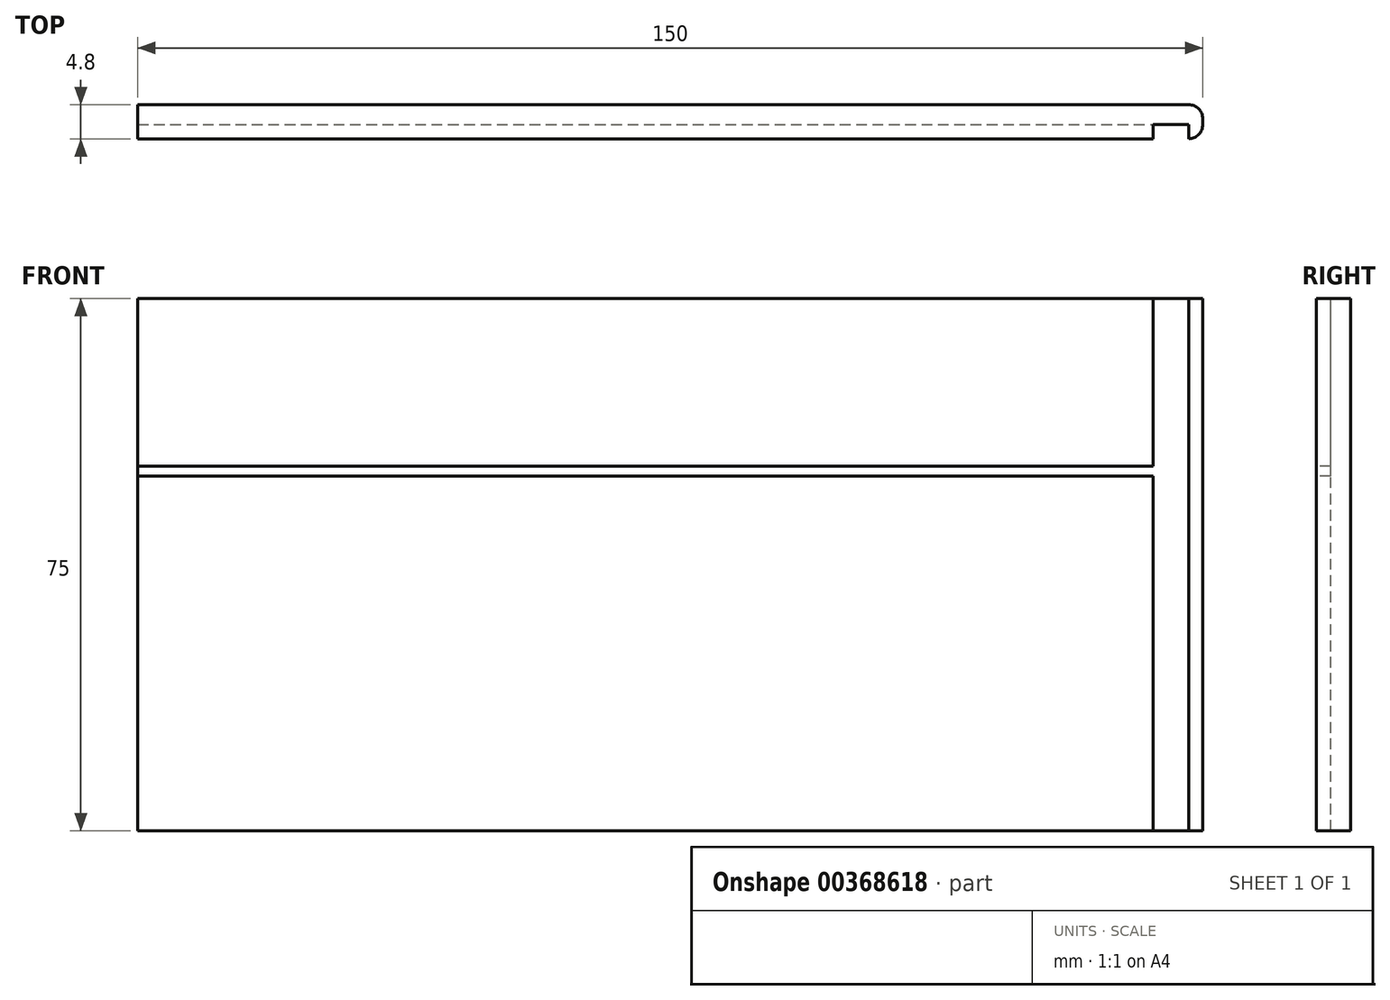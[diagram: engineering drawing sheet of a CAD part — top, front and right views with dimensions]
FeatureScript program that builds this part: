
annotation { "Feature Type Name" : "Feature", "Feature Type Description" : "" }
export const myFeature = defineFeature(function(context is Context, id is Id, definition is map)
    precondition{}
    {
        {
            var Q0;
            Q0=qCreatedBy(makeId("Front.planeOp"),FACE);
            var sketch = newSketch(context, id + "F0", { "sketchPlane" : qUnion([Q0])});
            skLineSegment(sketch, "E0.bottom", {"start": v(75, -37.5) * mm, "end": v(-75, -37.5) * mm});
            skLineSegment(sketch, "E0.top", {"start": v(75, 37.5) * mm, "end": v(-75, 37.5) * mm});
            skLineSegment(sketch, "E0.left", {"start": v(75, -37.5) * mm, "end": v(75, 37.5) * mm});
            skLineSegment(sketch, "E0.right", {"start": v(-75, -37.5) * mm, "end": v(-75, 37.5) * mm});
            skPoint(sketch, "E0.middle", {"position": v(0, 0) * mm});
            skSolve(sketch);
        }
        {
            var Q0;
            Q0=qSketchRegion(id+"F0",true);
            extrude(context, id + "F1", {"entities" : qUnion([Q0]), "depth" : 4.8 * mm});
        }
        {
            var Q0;
            Q0=makeQuery(id+"F1.opExtrude","CAP_FACE",FACE,{"disambiguationData":[OSD([sQuery(id+"F0.wireOp",EDGE,"E0.bottom"),sQuery(id+"F0.wireOp",EDGE,"E0.top"),sQuery(id+"F0.wireOp",EDGE,"E0.left"),sQuery(id+"F0.wireOp",EDGE,"E0.right")])],"isStart":false});
            var sketch = newSketch(context, id + "F2", { "sketchPlane" : qUnion([Q0])});
            skLineSegment(sketch, "E1.bottom", {"start": v(68, -37.5) * mm, "end": v(73, -37.5) * mm});
            skLineSegment(sketch, "E1.top", {"start": v(68, 37.5) * mm, "end": v(73, 37.5) * mm});
            skLineSegment(sketch, "E1.left", {"start": v(68, -37.5) * mm, "end": v(68, 37.5) * mm});
            skLineSegment(sketch, "E1.right", {"start": v(73, -37.5) * mm, "end": v(73, 37.5) * mm});
            skPoint(sketch, "E1.middle", {"position": v(70.5, 0) * mm});
            skLineSegment(sketch, "E2.bottom", {"start": v(-75, 13.9) * mm, "end": v(68, 13.9) * mm});
            skLineSegment(sketch, "E2.top", {"start": v(-75, 12.5) * mm, "end": v(68, 12.5) * mm});
            skLineSegment(sketch, "E2.left", {"start": v(-75, 13.9) * mm, "end": v(-75, 12.5) * mm});
            skLineSegment(sketch, "E2.right", {"start": v(68, 13.9) * mm, "end": v(68, 12.5) * mm});
            skSolve(sketch);
        }
        {
            var Q0;
            Q0=qSketchRegion(id+"F2",true);
            extrude(context, id + "F3", {"entities" : qUnion([Q0]), "operationType" : NewBodyOperationType.REMOVE, "oppositeDirection" : true, "depth" : 2 * mm});
        }
        {
            var Q0;
            Q0=makeQuery(id+"F1.opExtrude","CAP_EDGE",EDGE,{"disambiguationData":[OSD([sQuery(id+"F0.wireOp",EDGE,"E0.left")])],"isStart":true});
            var Q1;
            {var subQ0=sQuery(id+"F0.wireOp",EDGE,"E0.left");var subQ1=sQuery(id+"F0.wireOp",EDGE,"E0.top");var subQ3=makeQuery(id+"F1.opExtrude","CAP_EDGE",EDGE,{"disambiguationData":[OSD([subQ0])],"isStart":false});Q1=makeQuery(id+"F3.boolean.opBoolean","SPLIT",EDGE,{"disambiguationData":[TD([makeQuery(id+"F1.opExtrude","SWEPT_FACE",FACE,{"disambiguationData":[OSD([subQ1])]})])],"derivedFrom":subQ3});}
            fillet(context, id + "F4", {"entities" : qUnion([Q0, Q1]), "radius" : 2 * mm, "tangentPropagation" : true, "allowEdgeOverflow" : false});
        }
    });
